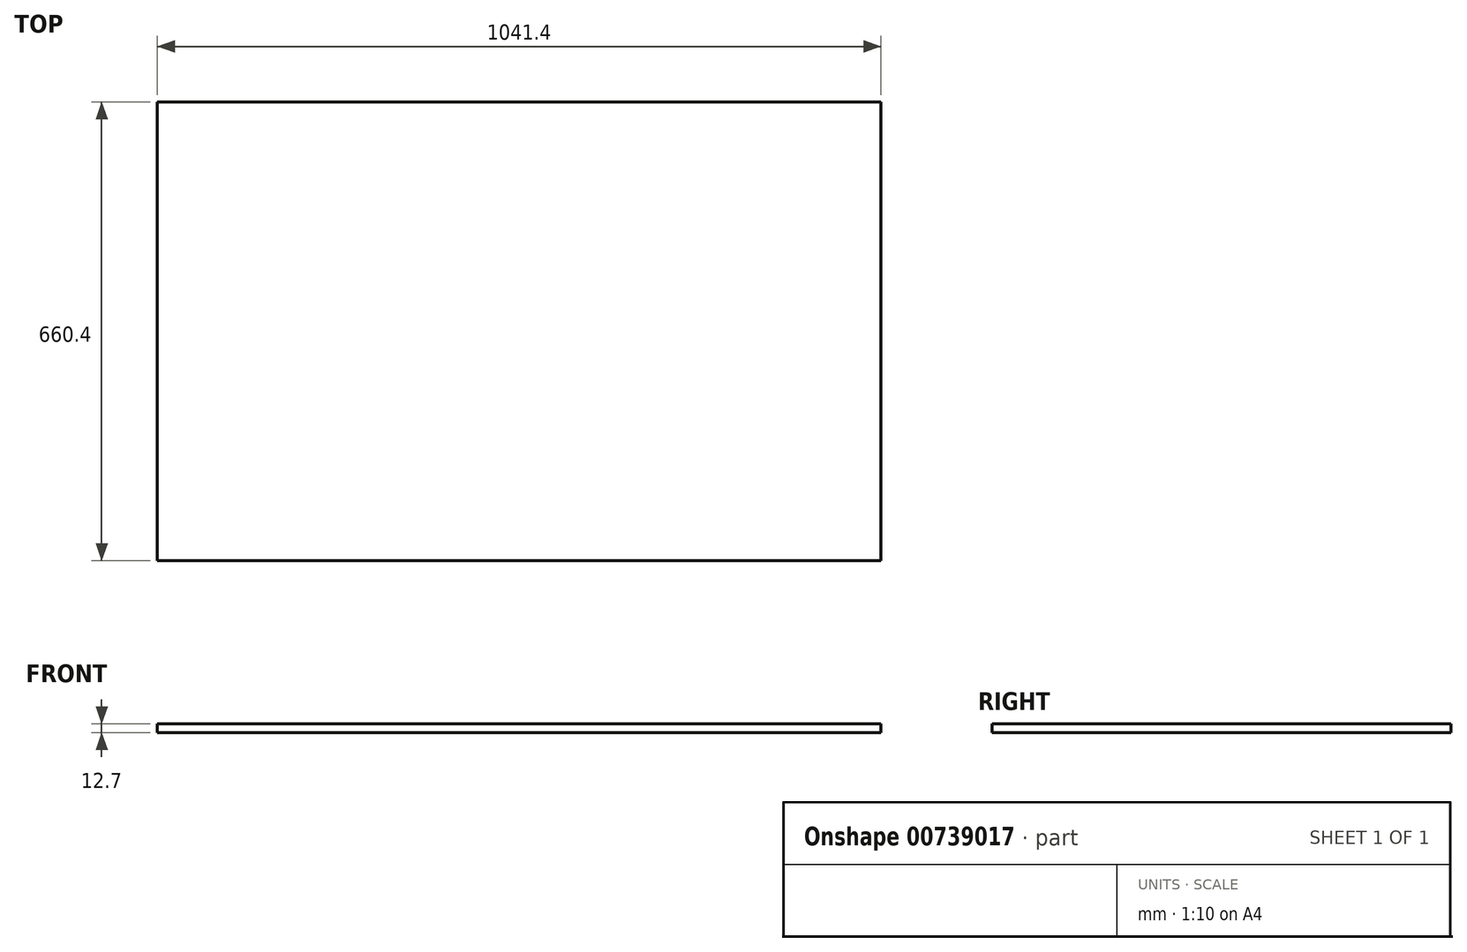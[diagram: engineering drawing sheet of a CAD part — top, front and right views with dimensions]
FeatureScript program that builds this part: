
annotation { "Feature Type Name" : "Feature", "Feature Type Description" : "" }
export const myFeature = defineFeature(function(context is Context, id is Id, definition is map)
    precondition{}
    {
        {
            var Q0;
            Q0=qCreatedBy(makeId("Top.planeOp"),FACE);
            var sketch = newSketch(context, id + "F0", { "sketchPlane" : qUnion([Q0])});
            skLineSegment(sketch, "E0.bottom", {"start": v(-461.37, 386.31) * mm, "end": v(580.03, 386.31) * mm});
            skLineSegment(sketch, "E0.top", {"start": v(-461.37, -274.09) * mm, "end": v(580.03, -274.09) * mm});
            skLineSegment(sketch, "E0.left", {"start": v(-461.37, 386.31) * mm, "end": v(-461.37, -274.09) * mm});
            skLineSegment(sketch, "E0.right", {"start": v(580.03, 386.31) * mm, "end": v(580.03, -274.09) * mm});
            skSolve(sketch);
        }
        {
            var Q0;
            Q0 = qSketchRegion(id + "F0", true);
            extrude(context, id + "F1", {"entities" : qUnion([Q0]), "depth" : 12.7 * mm, "offsetDistance" : 25.4 * mm});
        }
    });
